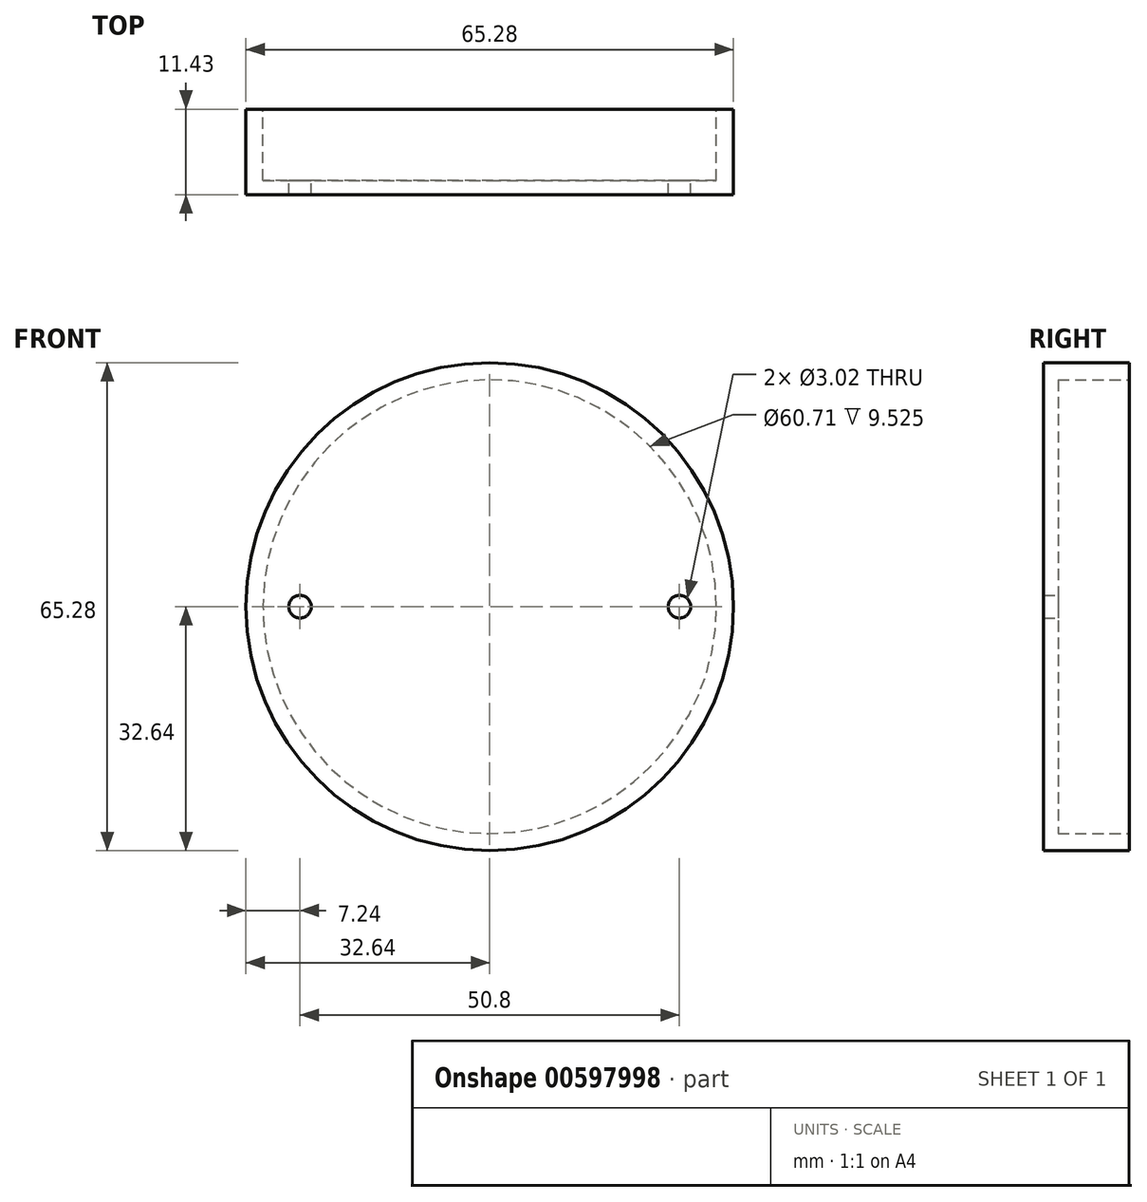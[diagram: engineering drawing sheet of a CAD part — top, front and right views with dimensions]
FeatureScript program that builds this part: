
annotation { "Feature Type Name" : "Feature", "Feature Type Description" : "" }
export const myFeature = defineFeature(function(context is Context, id is Id, definition is map)
    precondition{}
    {
        {
            var Q0;
            Q0=qCreatedBy(makeId("Front.planeOp"),FACE);
            var sketch = newSketch(context, id + "F0", { "sketchPlane" : qUnion([Q0])});
            skCircle(sketch, "E0", {"center": v(0, 0) * mm, "radius": 32.64 * mm});
            skSolve(sketch);
        }
        {
            var Q0;
            Q0=qSketchRegion(id+"F0",true);
            extrude(context, id + "F1", {"entities" : qUnion([Q0]), "depth" : 11.43 * mm, "offsetDistance" : 25.4 * mm});
        }
        {
            var Q0;
            Q0=makeQuery(id+"F1.opExtrude","CAP_FACE",FACE,{"disambiguationData":[OSD([sQuery(id+"F0.wireOp",EDGE,"E0")])],"isStart":true});
            var sketch = newSketch(context, id + "F2", { "sketchPlane" : qUnion([Q0])});
            skCircle(sketch, "E1", {"center": v(0, 0) * mm, "radius": 30.35 * mm});
            skSolve(sketch);
        }
        {
            var Q0;
            Q0=qSketchRegion(id+"F2",true);
            extrude(context, id + "F3", {"entities" : qUnion([Q0]), "operationType" : NewBodyOperationType.REMOVE, "oppositeDirection" : true, "depth" : 9.52 * mm, "offsetDistance" : 25.4 * mm});
        }
        {
            var Q0;
            Q0=makeQuery(id+"F3.boolean.opBoolean","COPY",FACE,{"derivedFrom":makeQuery(id+"F3.opExtrude","CAP_FACE",FACE,{"disambiguationData":[OSD([sQuery(id+"F2.wireOp",EDGE,"E1")])],"isStart":false})});
            var sketch = newSketch(context, id + "F4", { "sketchPlane" : qUnion([Q0])});
            skCircle(sketch, "E2", {"center": v(-25.4, 0) * mm, "radius": 1.51 * mm});
            skCircle(sketch, "E3", {"center": v(25.4, 0) * mm, "radius": 1.51 * mm});
            skSolve(sketch);
        }
        {
            var Q0;
            Q0=qSketchRegion(id+"F4",true);
            extrude(context, id + "F5", {"entities" : qUnion([Q0]), "operationType" : NewBodyOperationType.REMOVE, "oppositeDirection" : true, "depth" : 1.9 * mm, "offsetDistance" : 25.4 * mm});
        }
    });
